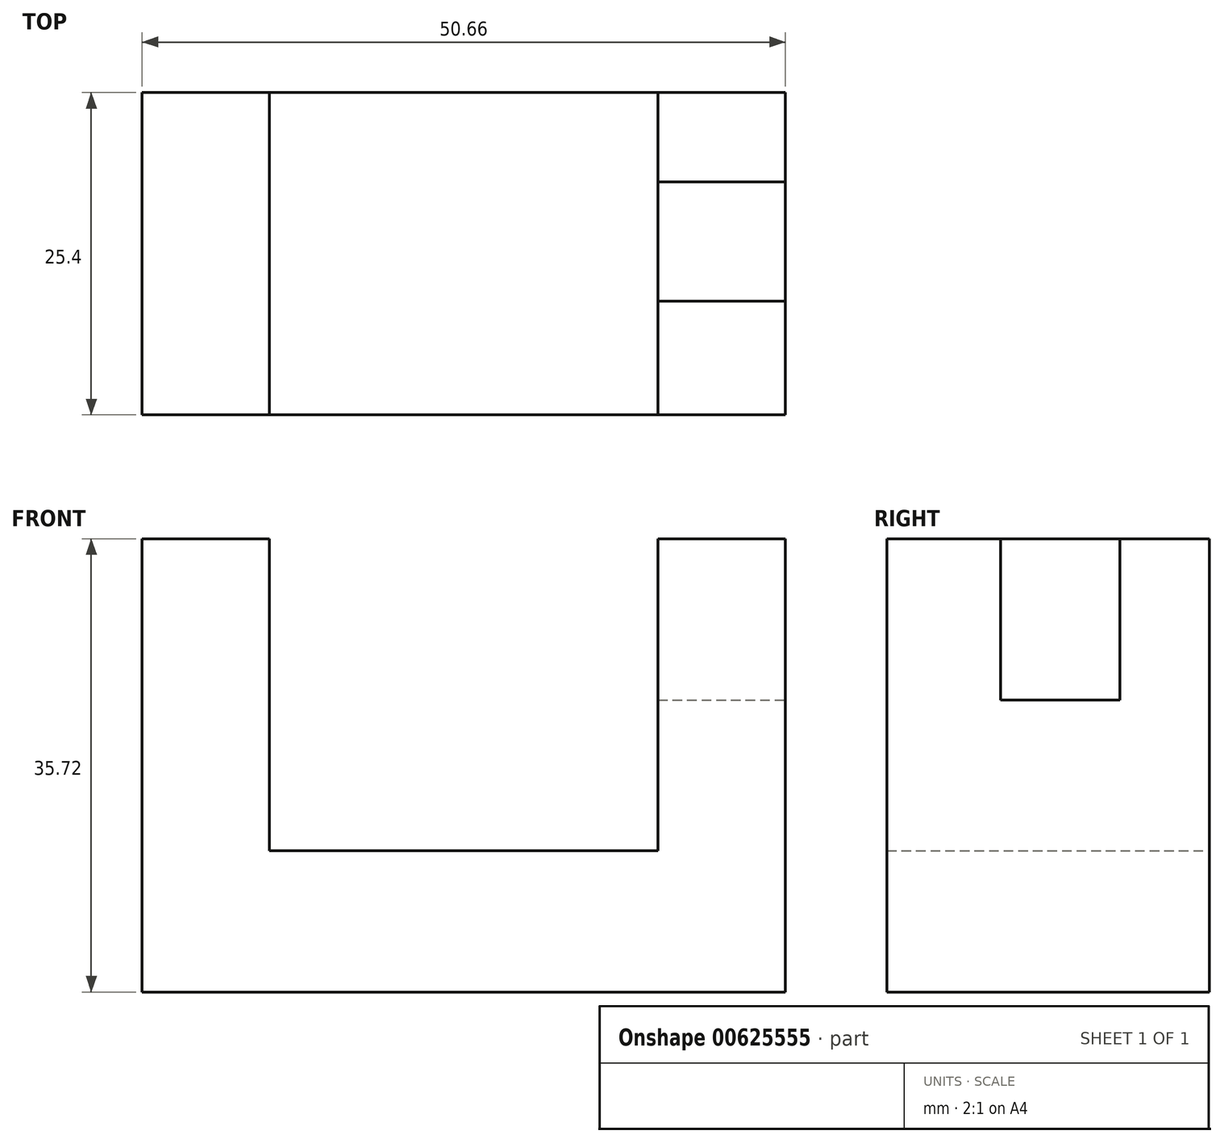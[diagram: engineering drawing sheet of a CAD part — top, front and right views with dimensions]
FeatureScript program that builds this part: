
annotation { "Feature Type Name" : "Feature", "Feature Type Description" : "" }
export const myFeature = defineFeature(function(context is Context, id is Id, definition is map)
    precondition{}
    {
        {
            var Q0;
            Q0=qCreatedBy(makeId("Front.planeOp"),FACE);
            var sketch = newSketch(context, id + "F0", { "sketchPlane" : qUnion([Q0])});
            skLineSegment(sketch, "E0.bottom", {"start": v(0, 0) * mm, "end": v(50.66, 0) * mm});
            skLineSegment(sketch, "E0.left", {"start": v(0, 0) * mm, "end": v(0, 35.72) * mm});
            skLineSegment(sketch, "E0.right", {"start": v(50.66, 0) * mm, "end": v(50.66, 35.72) * mm});
            skLineSegment(sketch, "E1.top", {"start": v(10.03, 11.12) * mm, "end": v(40.63, 11.12) * mm});
            skLineSegment(sketch, "E1.left", {"start": v(10.03, 35.72) * mm, "end": v(10.03, 11.12) * mm});
            skLineSegment(sketch, "E1.right", {"start": v(40.63, 35.72) * mm, "end": v(40.63, 11.12) * mm});
            skLineSegment(sketch, "E2.trimOffspring", {"start": v(40.63, 35.72) * mm, "end": v(50.66, 35.72) * mm});
            skLineSegment(sketch, "E3", {"start": v(0, 35.72) * mm, "end": v(10.03, 35.72) * mm});
            skSolve(sketch);
        }
        {
            var Q0;
            Q0 = qSketchRegion(id + "F0", true);
            extrude(context, id + "F1", {"entities" : qUnion([Q0]), "depth" : 25.4 * mm, "offsetDistance" : 25.4 * mm});
        }
        {
            var Q0;
            Q0=makeQuery(id+"F1.opExtrude","SWEPT_FACE",FACE,{"disambiguationData":[OSD([sQuery(id+"F0.wireOp",EDGE,"E2.trimOffspring")])]});
            var sketch = newSketch(context, id + "F2", { "sketchPlane" : qUnion([Q0])});
            skLineSegment(sketch, "E4.bottom", {"start": v(40.63, -7.05) * mm, "end": v(50.66, -7.05) * mm});
            skLineSegment(sketch, "E4.top", {"start": v(40.63, -16.44) * mm, "end": v(50.66, -16.44) * mm});
            skLineSegment(sketch, "E4.left", {"start": v(40.63, -7.05) * mm, "end": v(40.63, -16.44) * mm});
            skLineSegment(sketch, "E4.right", {"start": v(50.66, -7.05) * mm, "end": v(50.66, -16.44) * mm});
            skSolve(sketch);
        }
        {
            var Q0;
            Q0=makeQuery(id+"F2.imprint","IMPRINT",FACE,{"disambiguationData":[TD([[makeQuery(id+"F2.imprint","IMPRINT",EDGE,{"derivedFrom":sQuery(id+"F2.wireOp",EDGE,"E4.bottom")}),-1.0]])]});
            extrude(context, id + "F3", {"entities" : qUnion([Q0]), "operationType" : NewBodyOperationType.REMOVE, "oppositeDirection" : true, "depth" : 12.7 * mm, "offsetDistance" : 25.4 * mm});
        }
    });
